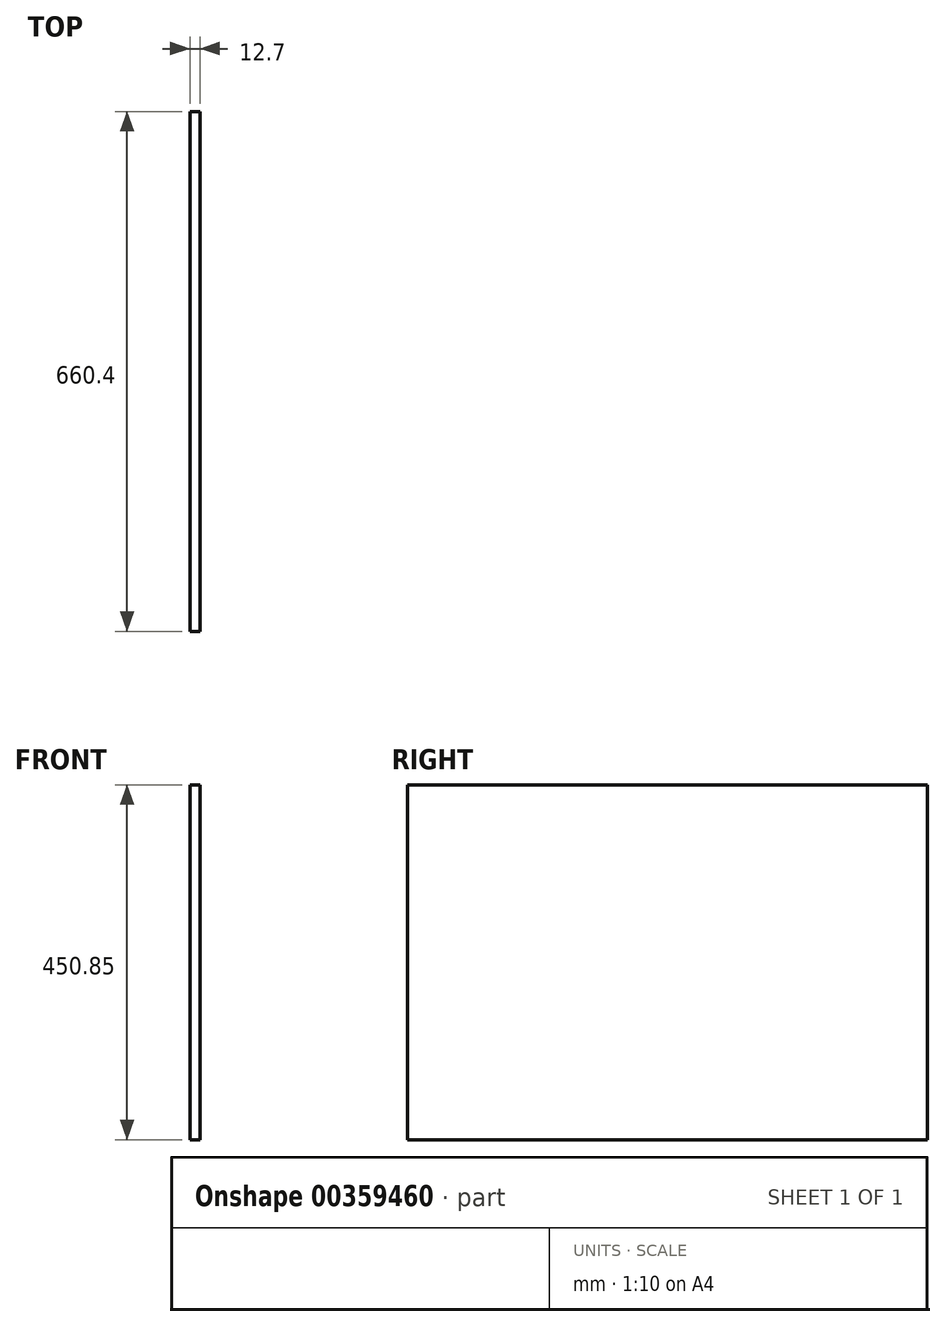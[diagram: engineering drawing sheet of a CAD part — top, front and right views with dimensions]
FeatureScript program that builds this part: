
annotation { "Feature Type Name" : "Feature", "Feature Type Description" : "" }
export const myFeature = defineFeature(function(context is Context, id is Id, definition is map)
    precondition{}
    {
        {
            var Q0;
            Q0=qCreatedBy(makeId("Right.planeOp"),FACE);
            var sketch = newSketch(context, id + "F0", { "sketchPlane" : qUnion([Q0])});
            skLineSegment(sketch, "E0.bottom", {"start": v(0, 0) * mm, "end": v(660.4, 0) * mm});
            skLineSegment(sketch, "E0.top", {"start": v(0, 450.85) * mm, "end": v(660.4, 450.85) * mm});
            skLineSegment(sketch, "E0.left", {"start": v(0, 0) * mm, "end": v(0, 450.85) * mm});
            skLineSegment(sketch, "E0.right", {"start": v(660.4, 0) * mm, "end": v(660.4, 450.85) * mm});
            skSolve(sketch);
        }
        {
            var Q0;
            Q0=makeQuery(id+"F0.imprint","IMPRINT",FACE,{"disambiguationData":[TD([[makeQuery(id+"F0.imprint","IMPRINT",EDGE,{"derivedFrom":sQuery(id+"F0.wireOp",EDGE,"E0.bottom")}),1.0]])]});
            extrude(context, id + "F1", {"entities" : qUnion([Q0]), "depth" : 12.7 * mm});
        }
    });
